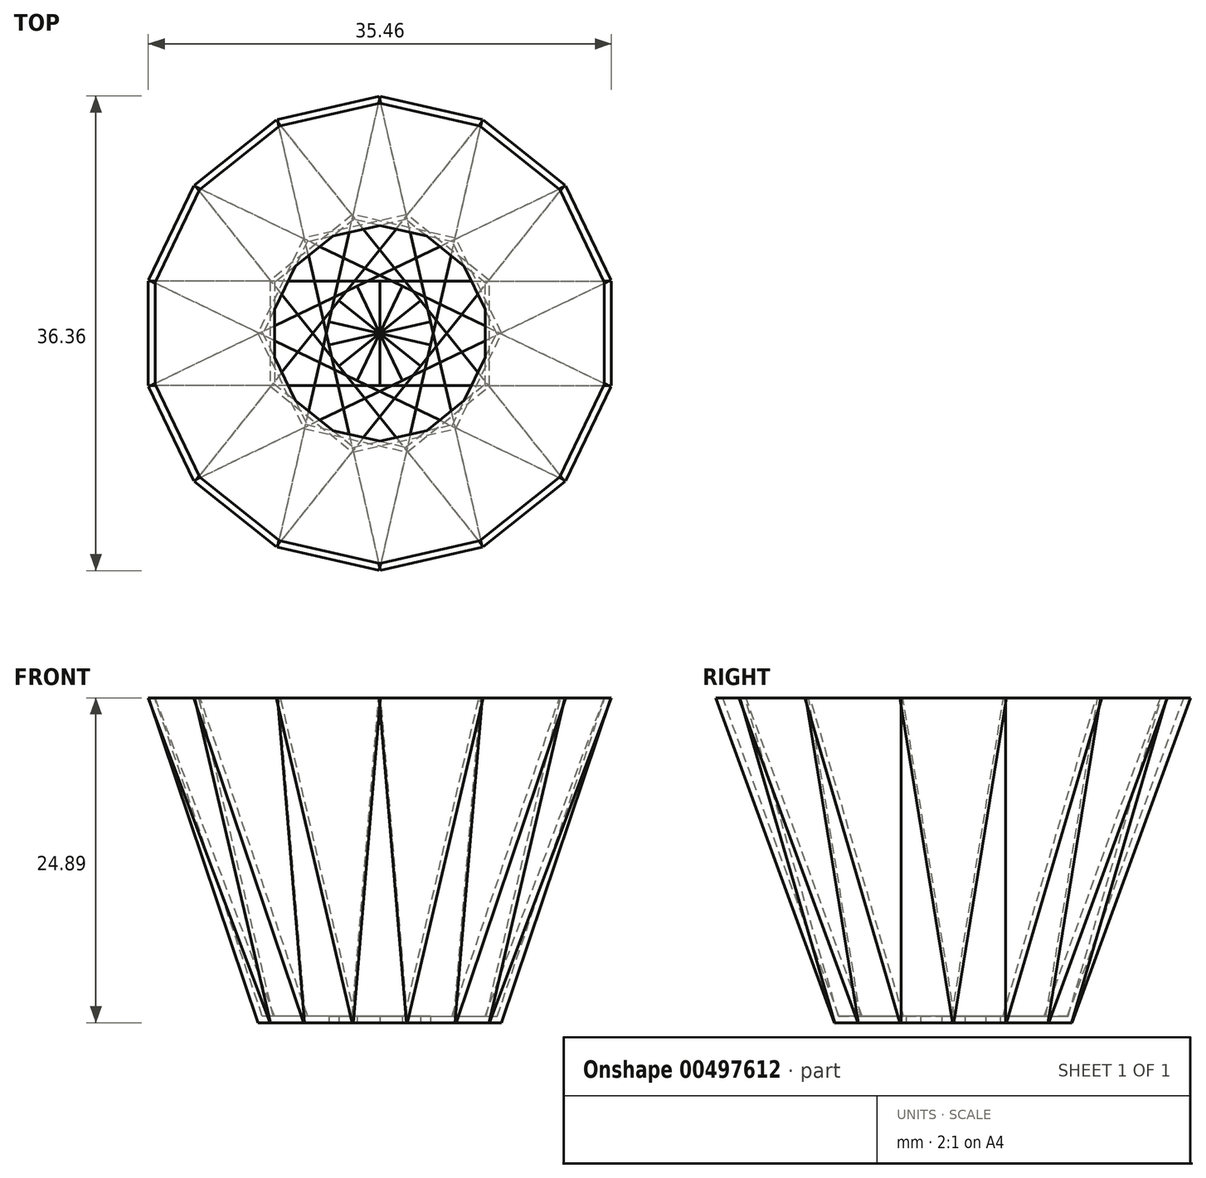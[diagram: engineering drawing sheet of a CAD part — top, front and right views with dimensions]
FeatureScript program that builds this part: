
annotation { "Feature Type Name" : "Feature", "Feature Type Description" : "" }
export const myFeature = defineFeature(function(context is Context, id is Id, definition is map)
    precondition{}
    {
        {
            var Q0;
            Q0=qCreatedBy(makeId("Front.planeOp"),FACE);
            var sketch = newSketch(context, id + "F0", { "sketchPlane" : qUnion([Q0])});
            skLineSegment(sketch, "E0", {"start": v(0, 0) * mm, "end": v(8.4, 0) * mm});
            skLineSegment(sketch, "E1", {"start": v(8.4, 0) * mm, "end": v(17.73, 24.89) * mm});
            skLineSegment(sketch, "E2", {"start": v(17.73, 24.89) * mm, "end": v(14.25, 52.02) * mm});
            skLineSegment(sketch, "E3.0", {"start": v(15.58, 25.14) * mm, "end": v(12.13, 52.02) * mm});
            skLineSegment(sketch, "E3.1", {"start": v(6.95, 2.1) * mm, "end": v(15.58, 25.14) * mm});
            skLineSegment(sketch, "E3.2", {"start": v(0, 2.1) * mm, "end": v(6.95, 2.1) * mm});
            skLineSegment(sketch, "E4", {"start": v(14.25, 52.02) * mm, "end": v(12.13, 52.02) * mm});
            skLineSegment(sketch, "E5", {"start": v(0, 2.1) * mm, "end": v(0, 0) * mm});
            skLineSegment(sketch, "E6", {"start": v(17.73, 24.89) * mm, "end": v(15.49, 24.89) * mm});
            skLineSegment(sketch, "E7.0", {"start": v(8.06, 0.5) * mm, "end": v(17.26, 25.06) * mm});
            skLineSegment(sketch, "E7.1", {"start": v(0, 0.5) * mm, "end": v(8.06, 0.5) * mm});
            skSolve(sketch);
        }
        {
            var Q0;
            Q0=makeQuery(id+"F0.imprint","IMPRINT",FACE,{"disambiguationData":[TD([[makeQuery(id+"F0.imprint","IMPRINT",EDGE,{"derivedFrom":sQuery(id+"F0.wireOp",EDGE,"E0")}),1.0]])]});
            extrude(context, id + "F1", {"entities" : qUnion([Q0]), "depth" : 4 * mm, "hasSecondDirection" : true, "secondDirectionOppositeDirection" : true, "secondDirectionDepth" : 4 * mm});
        }
        {
            var Q0;
            Q0=makeQuery(id+"F1.opExtrude","SWEPT_BODY",BODY,{"disambiguationData":[OSD([sQuery(id+"F0.wireOp",EDGE,"E0"),sQuery(id+"F0.wireOp",EDGE,"E1"),sQuery(id+"F0.wireOp",EDGE,"E2"),sQuery(id+"F0.wireOp",EDGE,"E3.0"),sQuery(id+"F0.wireOp",EDGE,"E3.1"),sQuery(id+"F0.wireOp",EDGE,"E3.2"),sQuery(id+"F0.wireOp",EDGE,"E4"),sQuery(id+"F0.wireOp",EDGE,"E5")])]});
            var Q1;
            Q1=sQuery(id+"F0.wireOp",EDGE,"E5");
            circularPattern(context, id + "F2", {"entities" : qUnion([Q0]), "axis" : qUnion([Q1]), "angle" : 360 * degree, "instanceCount" : 14, "equalSpace" : true});
        }
    });
